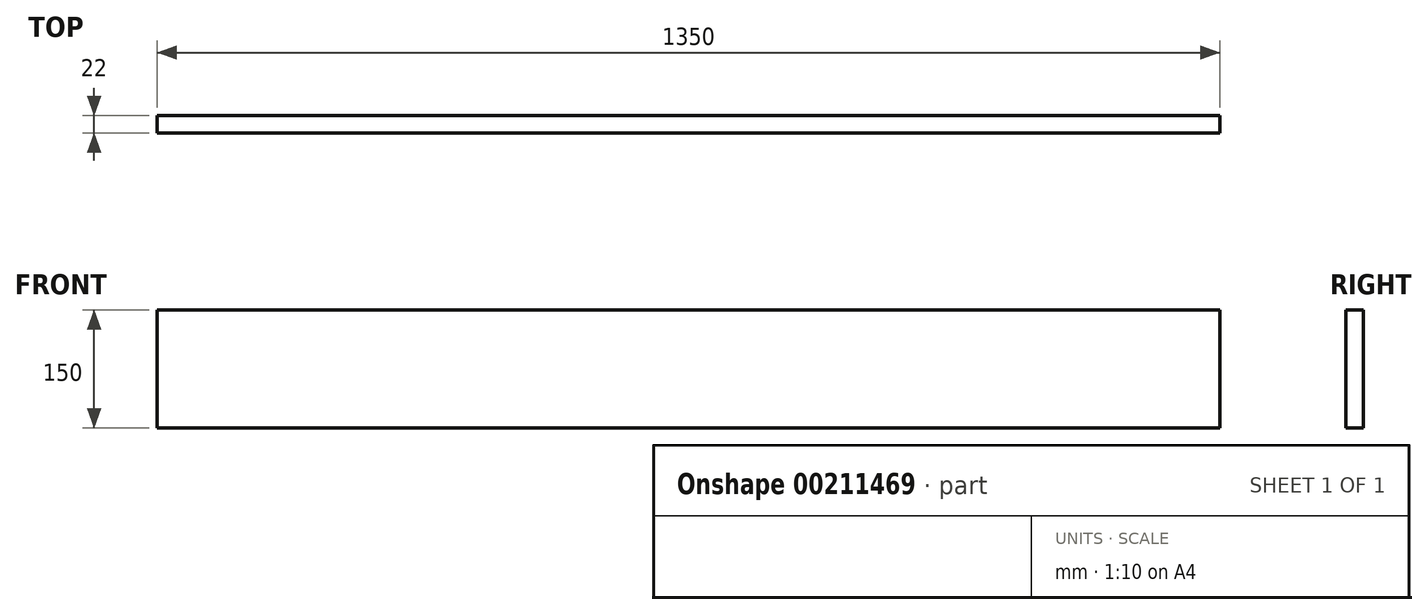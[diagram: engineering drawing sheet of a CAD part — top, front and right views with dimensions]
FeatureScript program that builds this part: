
annotation { "Feature Type Name" : "Feature", "Feature Type Description" : "" }
export const myFeature = defineFeature(function(context is Context, id is Id, definition is map)
    precondition{}
    {
        {
            var Q0;
            Q0=qCreatedBy(makeId("Front.planeOp"),FACE);
            var sketch = newSketch(context, id + "F0", { "sketchPlane" : qUnion([Q0])});
            skLineSegment(sketch, "E0.bottom", {"start": v(-675, 75) * mm, "end": v(675, 75) * mm});
            skLineSegment(sketch, "E0.top", {"start": v(-675, -75) * mm, "end": v(675, -75) * mm});
            skLineSegment(sketch, "E0.left", {"start": v(-675, 75) * mm, "end": v(-675, -75) * mm});
            skLineSegment(sketch, "E0.right", {"start": v(675, 75) * mm, "end": v(675, -75) * mm});
            skSolve(sketch);
        }
        {
            var Q0;
            Q0=qSketchRegion(id+"F0",true);
            extrude(context, id + "F1", {"entities" : qUnion([Q0]), "depth" : 22 * mm});
        }
    });
